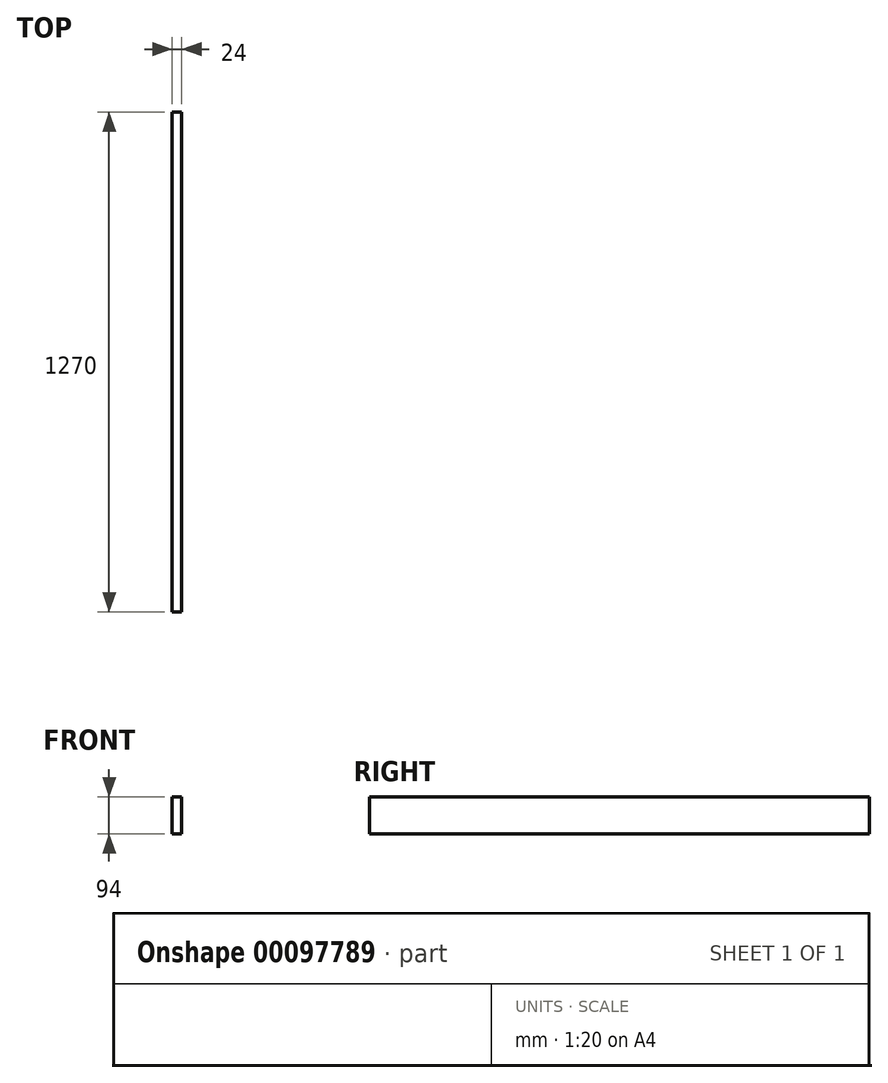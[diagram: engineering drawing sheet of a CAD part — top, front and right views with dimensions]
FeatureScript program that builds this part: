
annotation { "Feature Type Name" : "Feature", "Feature Type Description" : "" }
export const myFeature = defineFeature(function(context is Context, id is Id, definition is map)
    precondition{}
    {
        {
            var Q0;
            Q0=qCreatedBy(makeId("Front.planeOp"),FACE);
            var sketch = newSketch(context, id + "F0", { "sketchPlane" : qUnion([Q0])});
            skLineSegment(sketch, "E0.bottom", {"start": v(0, 0) * mm, "end": v(24, 0) * mm});
            skLineSegment(sketch, "E0.top", {"start": v(0, 94) * mm, "end": v(24, 94) * mm});
            skLineSegment(sketch, "E0.left", {"start": v(0, 0) * mm, "end": v(0, 94) * mm});
            skLineSegment(sketch, "E0.right", {"start": v(24, 0) * mm, "end": v(24, 94) * mm});
            skSolve(sketch);
        }
        {
            var Q0;
            Q0=qSketchRegion(id+"F0",true);
            extrude(context, id + "F1", {"entities" : qUnion([Q0]), "oppositeDirection" : true, "depth" : 1270 * mm});
        }
    });
